FCSTD DOCUMENT  (FreeCAD 0.15R4671 (Git))
Label: FullGraphicDisplayFrontCover
License: All rights reserved
LicenseURL: http://en.wikipedia.org/wiki/All_rights_reserved
objects: Sketcher::SketchObject×21, PartDesign::Pocket×16, Part::Feature×7, PartDesign::Pad×5, Mesh::Feature×1, PartDesign::Fillet×1
note: 71 computed .brp shape members not serialized (recipe doc carries the construction recipe); baked Part::Feature solids carry a one-line shape summary decoded from their .brp

FEATURE [Sketcher::SketchObject] Sketch
  Placement = pos=(-49.5,0,0) rot=(0.57735,0.57735,0.57735;2.0944rad)
  sketch-geometry (5):
    g0: LineSegment StartX=32.5 StartY=50 StartZ=0 EndX=32.5 EndY=-50 EndZ=0
    g1: LineSegment StartX=13 StartY=50 StartZ=0 EndX=-40 EndY=-41.5 EndZ=0
    g2: LineSegment StartX=-40 StartY=-41.5 StartZ=0 EndX=-40 EndY=-50 EndZ=0
    g3: LineSegment StartX=-40 StartY=-50 StartZ=0 EndX=32.5 EndY=-50 EndZ=0
    g4: LineSegment StartX=13 StartY=50 StartZ=0 EndX=32.5 EndY=50 EndZ=0
  constraints (8):
    c: Vertical(g0)
    c: DistanceY(g0,g0) = 100
    c: DistanceY(g-1,g0) = 50
    c: Coincident(g1,g2)
    c: Coincident(g1,g4)
    c: Coincident(g0,g4)
    c: Coincident(g2,g3)
    c: Coincident(g0,g3)
FEATURE [PartDesign::Pad] Pad
  Length = 100
  Length2 = 100
  Placement = pos=(-49.5,0,0) rot=(0.57735,0.57735,0.57735;2.0944rad)
  Sketch = -> Sketch
  Type = 0
FEATURE [Mesh::Feature] geetech_graphic_smart_controller
  Placement = pos=(47,-21,-38) rot=(0.447214,-0.447214,0.774597;1.82349rad)
FEATURE [Sketcher::SketchObject] Sketch001
  Placement = pos=(-49.5,-11.9518,6.92288) rot=(0.446776,0.446776,-0.775102;1.82285rad)
  Support = -> Pad [Face5]
  sketch-geometry (4):
    g0: LineSegment StartX=-34 StartY=88 StartZ=0 EndX=11.25 EndY=88 EndZ=0
    g1: LineSegment StartX=11.25 StartY=88 StartZ=0 EndX=11.25 EndY=12.5 EndZ=0
    g2: LineSegment StartX=11.25 StartY=12.5 StartZ=0 EndX=-34 EndY=12.5 EndZ=0
    g3: LineSegment StartX=-34 StartY=12.5 StartZ=0 EndX=-34 EndY=88 EndZ=0
  constraints (8):
    c: Coincident(g0,g1)
    c: Coincident(g1,g2)
    c: Coincident(g2,g3)
    c: Coincident(g3,g0)
    c: Horizontal(g0)
    c: Horizontal(g2)
    c: Vertical(g1)
    c: Vertical(g3)
FEATURE [PartDesign::Pocket] Pocket
  Length = 5
  Placement = pos=(-49.5,0,0) rot=(0.57735,0.57735,0.57735;2.0944rad)
  Sketch = -> Sketch001
  Type = 0
FEATURE [Sketcher::SketchObject] Sketch002
  Placement = pos=(50.5,0,0) rot=(0.57735,0.57735,0.57735;2.0944rad)
  Support = -> Pocket [Face5]
  sketch-geometry (4):
    g0: LineSegment StartX=6.25 StartY=9.25 StartZ=0 EndX=9 EndY=7.5 EndZ=0
    g1: LineSegment StartX=9 StartY=7.5 StartZ=0 EndX=-4.75 EndY=-16 EndZ=0
    g2: LineSegment StartX=-4.75 StartY=-16 StartZ=0 EndX=-7.5 EndY=-14.5 EndZ=0
    g3: LineSegment StartX=-7.5 StartY=-14.5 StartZ=0 EndX=6.25 EndY=9.25 EndZ=0
  constraints (4):
    c: Coincident(g0,g1)
    c: Coincident(g1,g2)
    c: Coincident(g2,g3)
    c: Coincident(g3,g0)
FEATURE [PartDesign::Pocket] Pocket001
  Length = 5
  Placement = pos=(-49.5,0,0) rot=(0.57735,0.57735,0.57735;2.0944rad)
  Sketch = -> Sketch002
  Type = 0
FEATURE [Sketcher::SketchObject] Sketch003
  Placement = pos=(-49.5,-11.9518,6.92288) rot=(0.446776,0.446776,-0.775102;1.82285rad)
  Support = -> Pocket001 [Face2]
  sketch-geometry (1):
    g0: Circle CenterX=32.75 CenterY=66.5 CenterZ=0 NormalX=0 NormalY=0 NormalZ=1 Radius=3.5
  constraints (1):
    c: Radius(g0) = 3.5
FEATURE [PartDesign::Pocket] Pocket002
  Length = 5
  Placement = pos=(-49.5,0,0) rot=(0.57735,0.57735,0.57735;2.0944rad)
  Sketch = -> Sketch003
  Type = 0
FEATURE [Sketcher::SketchObject] Sketch004
  Placement = pos=(50.5,0,0) rot=(0.57735,0.57735,0.57735;2.0944rad)
  Support = -> Pocket002 [Face5]
  sketch-geometry (6):
    g0: LineSegment StartX=30 StartY=51 StartZ=0 EndX=30 EndY=50 EndZ=0
    g1: LineSegment StartX=30 StartY=50 StartZ=0 EndX=-28 EndY=-50 EndZ=0
    g2: LineSegment StartX=-28 StartY=-50 StartZ=0 EndX=-28 EndY=-51 EndZ=0
    g3: LineSegment StartX=-28 StartY=-51 StartZ=0 EndX=34 EndY=-51 EndZ=0
    g4: LineSegment StartX=34 StartY=-51 StartZ=0 EndX=34 EndY=51 EndZ=0
    g5: LineSegment StartX=34 StartY=51 StartZ=0 EndX=30 EndY=51 EndZ=0
  constraints (11):
    c: Coincident(g1,g2)
    c: Coincident(g2,g3)
    c: Coincident(g3,g4)
    c: Coincident(g4,g5)
    c: Coincident(g0,g1)
    c: Coincident(g0,g5)
    c: Horizontal(g5)
    c: Vertical(g0)
    c: Vertical(g4)
    c: Vertical(g2)
    c: Horizontal(g3)
FEATURE [PartDesign::Pocket] Pocket003
  Length = 5
  Placement = pos=(-49.5,0,0) rot=(0.57735,0.57735,0.57735;2.0944rad)
  Sketch = -> Sketch004
  Type = 1
FEATURE [Sketcher::SketchObject] Sketch005
  Placement = pos=(-49.5,-11.9518,6.92288) rot=(0.446776,0.446776,-0.775102;1.82285rad)
  Support = -> Pocket003 [Face5]
  sketch-geometry (4):
    g0: LineSegment StartX=-59 StartY=1 StartZ=0 EndX=64 EndY=1 EndZ=0
    g1: LineSegment StartX=64 StartY=1 StartZ=0 EndX=64 EndY=-1 EndZ=0
    g2: LineSegment StartX=64 StartY=-1 StartZ=0 EndX=-59 EndY=-1 EndZ=0
    g3: LineSegment StartX=-59 StartY=-1 StartZ=0 EndX=-59 EndY=1 EndZ=0
  constraints (8):
    c: Coincident(g0,g1)
    c: Coincident(g1,g2)
    c: Coincident(g2,g3)
    c: Coincident(g3,g0)
    c: Horizontal(g0)
    c: Horizontal(g2)
    c: Vertical(g1)
    c: Vertical(g3)
FEATURE [PartDesign::Pocket] Pocket004
  Length = 5
  Placement = pos=(-49.5,0,0) rot=(0.57735,0.57735,0.57735;2.0944rad)
  Sketch = -> Sketch005
  Type = 1
FEATURE [Sketcher::SketchObject] Sketch006
  Placement = pos=(-48.5,0,0) rot=(-0.57735,-0.57735,0.57735;2.0944rad)
  Support = -> Pocket004 [Face2]
  sketch-geometry (5):
    g0: LineSegment StartX=32 StartY=-47.1429 StartZ=0 EndX=14.7932 EndY=-47.1429 EndZ=0
    g1: LineSegment StartX=14.7932 StartY=-47.1429 StartZ=0 EndX=-36.7559 EndY=42.1429 EndZ=0
    g2: LineSegment StartX=-36.7559 StartY=42.1429 StartZ=0 EndX=-36.7559 EndY=47 EndZ=0
    g3: LineSegment StartX=-36.7559 StartY=47 StartZ=0 EndX=-18 EndY=47 EndZ=0
    g4: LineSegment StartX=-18 StartY=47 StartZ=0 EndX=32 EndY=-47.1429 EndZ=0
  constraints (9):
    c: Coincident(g0,g1)
    c: Coincident(g1,g2)
    c: Coincident(g2,g3)
    c: Coincident(g3,g4)
    c: Coincident(g4,g0)
    c: Horizontal(g0)
    c: Horizontal(g3)
    c: Vertical(g2)
    c: Angle(g0,g1) = 2.0944
FEATURE [PartDesign::Pocket] Pocket005
  Length = 96
  Placement = pos=(-49.5,0,0) rot=(0.57735,0.57735,0.57735;2.0944rad)
  Sketch = -> Sketch006
  Type = 0
FEATURE [Sketcher::SketchObject] Sketch007
  Placement = pos=(-49.5,-9.31852,5.38005) rot=(0.654654,0.654654,0.377964;3.86433rad)
  Support = -> Pocket005 [Face11]
  sketch-geometry (4):
    g0: Circle CenterX=-40.8676 CenterY=6.08413 CenterZ=0 NormalX=0 NormalY=0 NormalZ=1 Radius=4.2
    g1: Circle CenterX=44.071 CenterY=6 CenterZ=0 NormalX=0 NormalY=0 NormalZ=1 Radius=4.2
    g2: Circle CenterX=44.0622 CenterY=93.943 CenterZ=0 NormalX=0 NormalY=0 NormalZ=1 Radius=4.2
    g3: Circle CenterX=-40.8785 CenterY=93.922 CenterZ=0 NormalX=0 NormalY=0 NormalZ=1 Radius=4.2
  constraints (4):
    c: Radius(g0) = 4.2
    c: Equal(g0,g1)
    c: Equal(g0,g2)
    c: Equal(g0,g3)
FEATURE [PartDesign::Pad] Pad001
  Length = 10
  Length2 = 100
  Placement = pos=(-49.5,0,0) rot=(0.57735,0.57735,0.57735;2.0944rad)
  Sketch = -> Sketch007
  Type = 0
FEATURE [Sketcher::SketchObject] Sketch008
  Placement = pos=(-48.5,0,0) rot=(0.57735,0.57735,-0.57735;4.18879rad)
  Support = -> Pad001 [Face2]
  sketch-geometry (4):
    g0: LineSegment StartX=13.75 StartY=-34.6313 StartZ=0 EndX=19.8066 EndY=-44.9063 EndZ=0
    g1: LineSegment StartX=19.8066 StartY=-44.9063 StartZ=0 EndX=25.25 EndY=-41.6078 EndZ=0
    g2: LineSegment StartX=25.25 StartY=-41.6078 StartZ=0 EndX=19.25 EndY=-31.25 EndZ=0
    g3: LineSegment StartX=19.25 StartY=-31.25 StartZ=0 EndX=13.75 EndY=-34.6313 EndZ=0
  constraints (4):
    c: Coincident(g0,g1)
    c: Coincident(g1,g2)
    c: Coincident(g2,g3)
    c: Coincident(g3,g0)
FEATURE [PartDesign::Pocket] Pocket006
  Length = 96
  Placement = pos=(-49.5,0,0) rot=(0.57735,0.57735,0.57735;2.0944rad)
  Sketch = -> Sketch008
  Type = 0
FEATURE [Sketcher::SketchObject] Sketch009
  Placement = pos=(-48.5,0,0) rot=(-0.57735,-0.57735,0.57735;2.0944rad)
  Support = -> Pocket006 [Face2]
  sketch-geometry (5):
    g0: LineSegment StartX=30 StartY=-50 StartZ=0 EndX=-28 EndY=50 EndZ=0
    g1: LineSegment StartX=-28 StartY=50 StartZ=0 EndX=-40 EndY=50 EndZ=0
    g2: LineSegment StartX=-40 StartY=50 StartZ=0 EndX=-40 EndY=41.5 EndZ=0
    g3: LineSegment StartX=-40 StartY=41.5 StartZ=0 EndX=13 EndY=-50 EndZ=0
    g4: LineSegment StartX=13 StartY=-50 StartZ=0 EndX=30 EndY=-50 EndZ=0
  constraints (5):
    c: Coincident(g0,g1)
    c: Coincident(g1,g2)
    c: Coincident(g2,g3)
    c: Coincident(g3,g4)
    c: Coincident(g4,g0)
FEATURE [PartDesign::Pad] Pad002
  Length = 3
  Length2 = 100
  Midplane = true
  Placement = pos=(-49.5,0,0) rot=(0.57735,0.57735,0.57735;2.0944rad)
  Sketch = -> Sketch009
  Type = 0
FEATURE [Part::Feature] Pad002001  label="Pad003"
  shape: bbox 100.5 x 70 x 100 mm, 32 faces (baked)
FEATURE [Sketcher::SketchObject] Sketch010
  Placement = pos=(0,-4.94515,2.91491) rot=(0,0.868273,0.496087;3.14159rad)
  Support = -> Pad002001 [Face20]
  sketch-geometry (2):
    g0: Circle CenterX=-44.4412 CenterY=44 CenterZ=0 NormalX=0 NormalY=0 NormalZ=1 Radius=1.5
    g1: Circle CenterX=43.4465 CenterY=44 CenterZ=0 NormalX=0 NormalY=0 NormalZ=1 Radius=1.5
  constraints (2):
    c: Radius(g0) = 1.5
    c: Equal(g0,g1)
FEATURE [PartDesign::Pocket] Pocket007
  Length = 6.4
  Sketch = -> Sketch010
  Type = 0
FEATURE [Sketcher::SketchObject] Sketch011
  Placement = pos=(0,-0.658268,0.380051) rot=(0,0.866025,0.5;3.14159rad)
  Support = -> Pocket007 [Face23]
  sketch-geometry (2):
    g0: Circle CenterX=-44.4338 CenterY=-40.8723 CenterZ=0 NormalX=0 NormalY=0 NormalZ=1 Radius=1.5
    g1: Circle CenterX=43.4318 CenterY=-40.9014 CenterZ=0 NormalX=0 NormalY=0 NormalZ=1 Radius=1.5
  constraints (2):
    c: Radius(g0) = 1.5
    c: Equal(g0,g1)
FEATURE [PartDesign::Pocket] Pocket008
  Length = 6.4
  Sketch = -> Sketch011
  Type = 0
FEATURE [Sketcher::SketchObject] Sketch012
  Placement = pos=(0,0.748279,-0.434002) rot=(0,0.866521,0.49914;3.14159rad)
  Support = -> Pocket008 [Face2]
  sketch-geometry (2):
    g0: Circle CenterX=-44.4463 CenterY=-40.8837 CenterZ=0 NormalX=0 NormalY=0 NormalZ=1 Radius=3.3
    g1: Circle CenterX=43.4235 CenterY=-40.9007 CenterZ=0 NormalX=0 NormalY=0 NormalZ=1 Radius=3.3
  constraints (2):
    c: Radius(g0) = 3.3
    c: Radius(g1) = 3.3
FEATURE [PartDesign::Pocket] Pocket009
  Length = 1
  Sketch = -> Sketch012
  Type = 0
FEATURE [Sketcher::SketchObject] Sketch013
  Placement = pos=(0,0.748279,-0.434002) rot=(0,0.866521,0.49914;3.14159rad)
  Support = -> Pocket009 [Face2]
  sketch-geometry (1):
    g0: Circle CenterX=-44.5 CenterY=44 CenterZ=0 NormalX=0 NormalY=0 NormalZ=1 Radius=3.3
  constraints (1):
    c: Radius(g0) = 3.3
FEATURE [PartDesign::Pocket] Pocket010
  Length = 5
  Sketch = -> Sketch013
  Type = 0
FEATURE [Part::Feature] Pocket010001  label="Pocket011"
  shape: bbox 100.5 x 70 x 100 mm, 44 faces (baked)
FEATURE [Sketcher::SketchObject] Sketch014
  Placement = pos=(0,-9.35582,5.41922) rot=(1,0,0;1.04578rad)
  Support = -> Pocket010001 [Face36]
  sketch-geometry (4):
    g0: LineSegment StartX=-37 StartY=34 StartZ=0 EndX=38.5 EndY=34 EndZ=0
    g1: LineSegment StartX=38.5 StartY=34 StartZ=0 EndX=38.5 EndY=-11.25 EndZ=0
    g2: LineSegment StartX=38.5 StartY=-11.25 StartZ=0 EndX=-37 EndY=-11.25 EndZ=0
    g3: LineSegment StartX=-37 StartY=-11.25 StartZ=0 EndX=-37 EndY=34 EndZ=0
  constraints (8):
    c: Coincident(g0,g1)
    c: Coincident(g1,g2)
    c: Coincident(g2,g3)
    c: Coincident(g3,g0)
    c: Horizontal(g0)
    c: Horizontal(g2)
    c: Vertical(g1)
    c: Vertical(g3)
FEATURE [PartDesign::Pocket] Pocket010002
  Length = 5
  Sketch = -> Sketch014
  Type = 0
FEATURE [Part::Feature] Part__Feature001  label="FullGraphicDisplayBackCover"
  Placement = pos=(0,37,0) rot=(0,0,1;0rad)
  shape: bbox 120.7 x 77.07 x 115.7 mm, 102 faces (baked)
FEATURE [PartDesign::Fillet] Fillet
  Base = -> Pocket010002 [Edge27,Edge2,Edge44,Edge5,Edge36,Edge32,Edge28,Edge35,Edge4,Edge3,Edge31]
  Radius = 2
FEATURE [Sketcher::SketchObject] Sketch015
  Placement = pos=(0,-11.9518,6.92288) rot=(1,0,0;1.04578rad)
  Support = -> Fillet [Face23]
  sketch-geometry (28):
    g0: ArcOfCircle CenterX=-24.25 CenterY=-34.5 CenterZ=0 NormalX=0 NormalY=0 NormalZ=1 Radius=0.5 StartAngle=1.5708 EndAngle=4.71239
    g1: ArcOfCircle CenterX=-11.75 CenterY=-34.5 CenterZ=0 NormalX=0 NormalY=0 NormalZ=1 Radius=0.5 StartAngle=4.71239 EndAngle=7.85398
    g2: LineSegment StartX=-24.25 StartY=-35 StartZ=0 EndX=-11.75 EndY=-35 EndZ=0
    g3: LineSegment StartX=-24.25 StartY=-34 StartZ=0 EndX=-11.75 EndY=-34 EndZ=0
    g4: ArcOfCircle CenterX=-23.5 CenterY=-32.75 CenterZ=0 NormalX=0 NormalY=0 NormalZ=1 Radius=0.5 StartAngle=1.5708 EndAngle=4.71239
    g5: ArcOfCircle CenterX=-12.5 CenterY=-32.75 CenterZ=0 NormalX=0 NormalY=0 NormalZ=1 Radius=0.5 StartAngle=4.71239 EndAngle=7.85398
    g6: LineSegment StartX=-23.5 StartY=-33.25 StartZ=0 EndX=-12.5 EndY=-33.25 EndZ=0
    g7: LineSegment StartX=-23.5 StartY=-32.25 StartZ=0 EndX=-12.5 EndY=-32.25 EndZ=0
    g8: ArcOfCircle CenterX=-22.5 CenterY=-31 CenterZ=0 NormalX=0 NormalY=0 NormalZ=1 Radius=0.5 StartAngle=1.5708 EndAngle=4.71239
    g9: ArcOfCircle CenterX=-13.5 CenterY=-31 CenterZ=0 NormalX=0 NormalY=0 NormalZ=1 Radius=0.5 StartAngle=4.71239 EndAngle=7.85398
    g10: LineSegment StartX=-22.5 StartY=-31.5 StartZ=0 EndX=-13.5 EndY=-31.5 EndZ=0
    g11: LineSegment StartX=-22.5 StartY=-30.5 StartZ=0 EndX=-13.5 EndY=-30.5 EndZ=0
    g12: ArcOfCircle CenterX=-20.5 CenterY=-29.25 CenterZ=0 NormalX=0 NormalY=0 NormalZ=1 Radius=0.5 StartAngle=1.5708 EndAngle=4.71239
    g13: ArcOfCircle CenterX=-15.5 CenterY=-29.25 CenterZ=0 NormalX=0 NormalY=0 NormalZ=1 Radius=0.5 StartAngle=4.71239 EndAngle=7.85398
    g14: LineSegment StartX=-20.5 StartY=-29.75 StartZ=0 EndX=-15.5 EndY=-29.75 EndZ=0
    g15: LineSegment StartX=-20.5 StartY=-28.75 StartZ=0 EndX=-15.5 EndY=-28.75 EndZ=0
    g16: ArcOfCircle CenterX=-23.5 CenterY=-36.25 CenterZ=0 NormalX=0 NormalY=0 NormalZ=1 Radius=0.5 StartAngle=1.5708 EndAngle=4.71239
    g17: ArcOfCircle CenterX=-12.5 CenterY=-36.25 CenterZ=0 NormalX=0 NormalY=0 NormalZ=1 Radius=0.5 StartAngle=4.71239 EndAngle=7.85398
    g18: LineSegment StartX=-23.5 StartY=-36.75 StartZ=0 EndX=-12.5 EndY=-36.75 EndZ=0
    g19: LineSegment StartX=-23.5 StartY=-35.75 StartZ=0 EndX=-12.5 EndY=-35.75 EndZ=0
    g20: ArcOfCircle CenterX=-13.5 CenterY=-38 CenterZ=0 NormalX=0 NormalY=0 NormalZ=1 Radius=0.5 StartAngle=4.71239 EndAngle=7.85398
    g21: ArcOfCircle CenterX=-22.5 CenterY=-38 CenterZ=0 NormalX=0 NormalY=0 NormalZ=1 Radius=0.5 StartAngle=1.5708 EndAngle=4.71239
    g22: LineSegment StartX=-13.5 StartY=-37.5 StartZ=0 EndX=-22.5 EndY=-37.5 EndZ=0
    g23: LineSegment StartX=-13.5 StartY=-38.5 StartZ=0 EndX=-22.5 EndY=-38.5 EndZ=0
    g24: ArcOfCircle CenterX=-20.5747 CenterY=-39.75 CenterZ=0 NormalX=0 NormalY=0 NormalZ=1 Radius=0.5 StartAngle=1.5708 EndAngle=4.71239
    g25: ArcOfCircle CenterX=-15.5 CenterY=-39.75 CenterZ=0 NormalX=0 NormalY=0 NormalZ=1 Radius=0.5 StartAngle=4.71239 EndAngle=7.85398
    g26: LineSegment StartX=-20.5747 StartY=-40.25 StartZ=0 EndX=-15.5 EndY=-40.25 EndZ=0
    g27: LineSegment StartX=-20.5747 StartY=-39.25 StartZ=0 EndX=-15.5 EndY=-39.25 EndZ=0
  constraints (42):
    c: Tangent(g0,g3) = 1.5708
    c: Tangent(g0,g2) = -1.5708
    c: Tangent(g2,g1) = -1.5708
    c: Tangent(g3,g1) = 1.5708
    c: Horizontal(g2)
    c: Equal(g0,g1)
    c: Tangent(g4,g7) = 1.5708
    c: Tangent(g4,g6) = -1.5708
    c: Tangent(g6,g5) = -1.5708
    c: Tangent(g7,g5) = 1.5708
    c: Horizontal(g6)
    c: Equal(g4,g5)
    c: Tangent(g8,g11) = 1.5708
    c: Tangent(g8,g10) = -1.5708
    c: Tangent(g10,g9) = -1.5708
    c: Tangent(g11,g9) = 1.5708
    c: Horizontal(g10)
    c: Equal(g8,g9)
    c: Tangent(g12,g15) = 1.5708
    c: Tangent(g12,g14) = -1.5708
    c: Tangent(g14,g13) = -1.5708
    c: Tangent(g15,g13) = 1.5708
    c: Horizontal(g14)
    c: Equal(g12,g13)
    c: Tangent(g16,g19) = 1.5708
    c: Tangent(g16,g18) = -1.5708
    c: Tangent(g18,g17) = -1.5708
    c: Tangent(g19,g17) = 1.5708
    c: Horizontal(g18)
    c: Equal(g16,g17)
    c: Tangent(g20,g23) = 1.5708
    c: Tangent(g20,g22) = -1.5708
    c: Tangent(g22,g21) = -1.5708
    c: Tangent(g23,g21) = 1.5708
    c: Horizontal(g22)
    c: Equal(g20,g21)
    c: Tangent(g24,g27) = 1.5708
    c: Tangent(g24,g26) = -1.5708
    c: Tangent(g26,g25) = -1.5708
    c: Tangent(g27,g25) = 1.5708
    c: Horizontal(g26)
    c: Equal(g24,g25)
FEATURE [PartDesign::Pocket] Pocket010003  label="SpeakerCutout"
  Length = 5
  Sketch = -> Sketch015
  Type = 1
FEATURE [Sketcher::SketchObject] Sketch016
  Placement = pos=(0,-11.9518,6.92288) rot=(1,0,0;1.04578rad)
  Support = -> Pocket010003 [Face23]
  sketch-geometry (2):
    g0: Circle CenterX=3 CenterY=-35.8517 CenterZ=0 NormalX=0 NormalY=0 NormalZ=1 Radius=3.5
    g1: Circle CenterX=35.8834 CenterY=-35.8517 CenterZ=0 NormalX=0 NormalY=0 NormalZ=1 Radius=3.5
  constraints (3):
    c: DistanceY(g0,g1) = 0
    c: Radius(g0) = 3.5
    c: Equal(g0,g1)
FEATURE [PartDesign::Pocket] Pocket010004
  Length = 5
  Sketch = -> Sketch016
  Type = 1
FEATURE [Part::Feature] Part__Feature  label="PushButton"
  Placement = pos=(35.9,-26.6,-26) rot=(1,0,0;1.0472rad)
  shape: bbox 12 x 14.57 x 16.7 mm, 34 faces (baked)
FEATURE [Sketcher::SketchObject] Sketch017
  Placement = pos=(0,-9.31852,5.38005) rot=(0,0.866025,0.5;3.14159rad)
  Support = -> Pocket010004 [Face34]
  sketch-geometry (4):
    g0: Circle CenterX=-35.8753 CenterY=-28.8272 CenterZ=0 NormalX=0 NormalY=0 NormalZ=1 Radius=2.2
    g1: Circle CenterX=-35.9065 CenterY=-42.8293 CenterZ=0 NormalX=0 NormalY=0 NormalZ=1 Radius=2.2
    g2: Circle CenterX=-2.915 CenterY=-28.8117 CenterZ=0 NormalX=0 NormalY=0 NormalZ=1 Radius=2.2
    g3: Circle CenterX=-2.91353 CenterY=-42.8404 CenterZ=0 NormalX=0 NormalY=0 NormalZ=1 Radius=2.22815
  constraints (3):
    c: Radius(g1) = 2.2
    c: Radius(g0) = 2.2
    c: Radius(g2) = 2.2
FEATURE [Part::Feature] Part__Feature002  label="PushButton001"
  Placement = pos=(2.9,-26.6,-26) rot=(1,0,0;1.0472rad)
  shape: bbox 12 x 14.57 x 16.7 mm, 34 faces (baked)
FEATURE [PartDesign::Pad] Pad002002
  Length = 1.75
  Length2 = 100
  Sketch = -> Sketch017
  Type = 0
FEATURE [Sketcher::SketchObject] Sketch018
  Placement = pos=(0,0,-50) rot=(1,0,0;3.14159rad)
  Support = -> Pad002002 [Face12]
  sketch-geometry (1):
    g0: Circle CenterX=0 CenterY=32 CenterZ=0 NormalX=0 NormalY=0 NormalZ=1 Radius=1.8
  constraints (1):
    c: Radius(g0) = 1.8
FEATURE [PartDesign::Pocket] Pocket010005
  Length = 4
  Sketch = -> Sketch018
  Type = 0
FEATURE [Sketcher::SketchObject] Sketch019
  Placement = pos=(0,-7.80298,4.50505) rot=(0,0.866025,0.5;3.14159rad)
  Support = -> Pocket010005 [Face96]
  sketch-geometry (4):
    g0: Circle CenterX=-35.91 CenterY=-28.8246 CenterZ=0 NormalX=0 NormalY=0 NormalZ=1 Radius=0.8
    g1: Circle CenterX=-35.9009 CenterY=-42.8088 CenterZ=0 NormalX=0 NormalY=0 NormalZ=1 Radius=0.8
    g2: Circle CenterX=-2.89811 CenterY=-28.8227 CenterZ=0 NormalX=0 NormalY=0 NormalZ=1 Radius=0.8
    g3: Circle CenterX=-2.90211 CenterY=-42.8288 CenterZ=0 NormalX=0 NormalY=0 NormalZ=1 Radius=0.8
  constraints (4):
    c: Radius(g3) = 0.8
    c: Equal(g3,g2)
    c: Equal(g3,g1)
    c: Equal(g3,g0)
FEATURE [PartDesign::Pad] Pad002003
  Length = 3
  Length2 = 100
  Sketch = -> Sketch019
  Type = 0
FEATURE [Part::Feature] Pad002004  label="FullGraphicDisplayFrontCover_WrongDisplaySize"
  shape: bbox 100.5 x 70 x 100 mm, 107 faces (baked)
FEATURE [Part::Feature] Part__Feature003  label="Knob"
  Placement = pos=(0,0,0) rot=(-1,0,0;0.523599rad)
  shape: bbox 22.2 x 18.36 x 22.12 mm, 15 faces (baked)
FEATURE [Sketcher::SketchObject] Sketch020
  Placement = pos=(0,-11.9518,6.92288) rot=(1,0,0;1.04578rad)
  Support = -> Pad002004 [Face23]
  sketch-geometry (4):
    g0: LineSegment StartX=-38.75 StartY=37 StartZ=0 EndX=40.25 EndY=37 EndZ=0
    g1: LineSegment StartX=40.25 StartY=37 StartZ=0 EndX=40.25 EndY=-14.5 EndZ=0
    g2: LineSegment StartX=40.25 StartY=-14.5 StartZ=0 EndX=-38.75 EndY=-14.5 EndZ=0
    g3: LineSegment StartX=-38.75 StartY=-14.5 StartZ=0 EndX=-38.75 EndY=37 EndZ=0
  constraints (10):
    c: Coincident(g0,g1)
    c: Coincident(g1,g2)
    c: Coincident(g2,g3)
    c: Coincident(g3,g0)
    c: Horizontal(g0)
    c: Horizontal(g2)
    c: Vertical(g1)
    c: Vertical(g3)
    c: DistanceY(g0,g2) = -51.5
    c: DistanceX(g0,g0) = 79
FEATURE [PartDesign::Pocket] Pocket010006  label="FullGraphicDisplayFrontCover"
  Length = 7
  Sketch = -> Sketch020
  Type = 0
